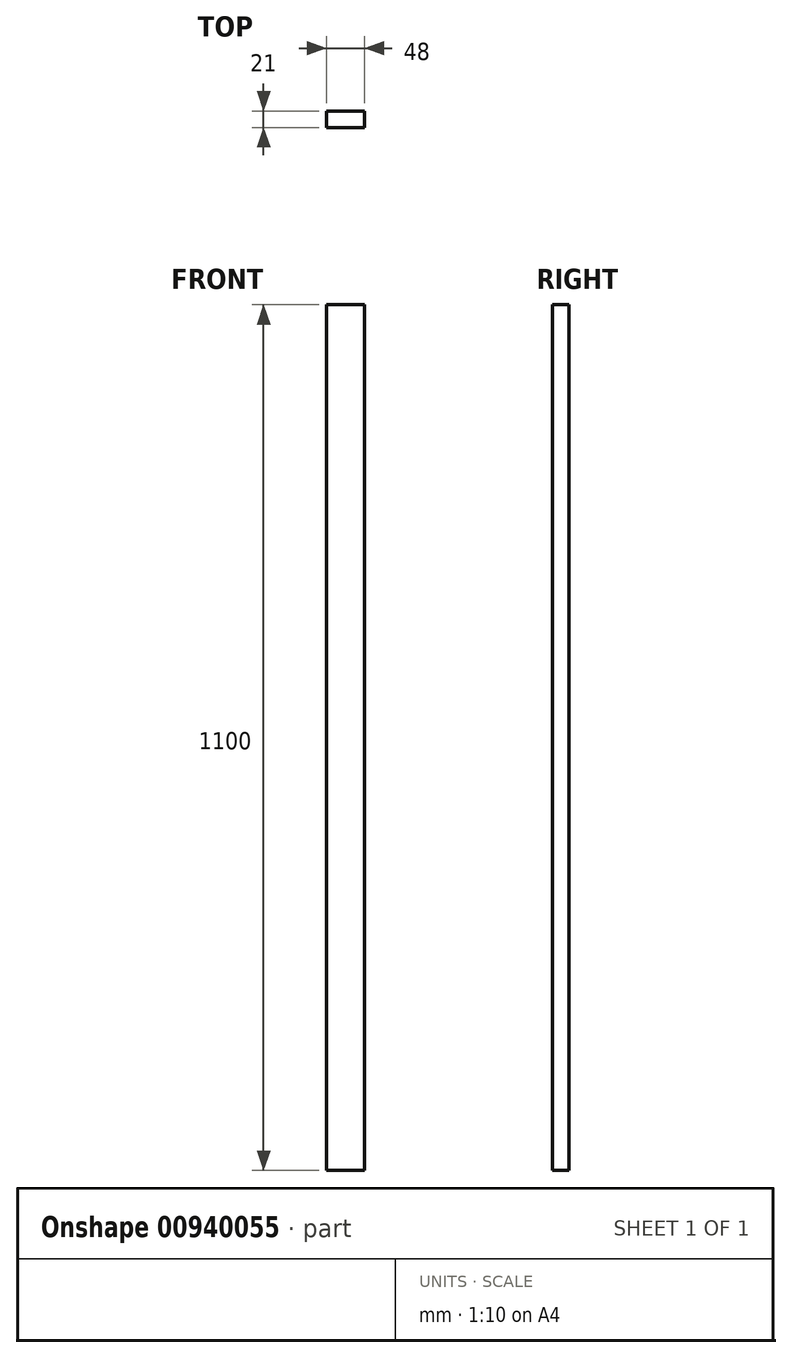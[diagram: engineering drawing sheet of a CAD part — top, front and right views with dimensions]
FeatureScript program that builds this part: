
annotation { "Feature Type Name" : "Feature", "Feature Type Description" : "" }
export const myFeature = defineFeature(function(context is Context, id is Id, definition is map)
    precondition{}
    {
        {
            var Q0;
            Q0=qCreatedBy(makeId("Top.planeOp"),FACE);
            var sketch = newSketch(context, id + "F0", { "sketchPlane" : qUnion([Q0])});
            skLineSegment(sketch, "E0.bottom", {"start": v(24, 10.5) * mm, "end": v(-24, 10.5) * mm});
            skLineSegment(sketch, "E0.top", {"start": v(24, -10.5) * mm, "end": v(-24, -10.5) * mm});
            skLineSegment(sketch, "E0.left", {"start": v(24, 10.5) * mm, "end": v(24, -10.5) * mm});
            skLineSegment(sketch, "E0.right", {"start": v(-24, 10.5) * mm, "end": v(-24, -10.5) * mm});
            skPoint(sketch, "E0.middle", {"position": v(0, 0) * mm});
            skSolve(sketch);
        }
        {
            var Q0;
            Q0 = qSketchRegion(id + "F0", true);
            extrude(context, id + "F1", {"entities" : qUnion([Q0]), "depth" : 1100 * mm, "offsetDistance" : 25 * mm});
        }
    });
